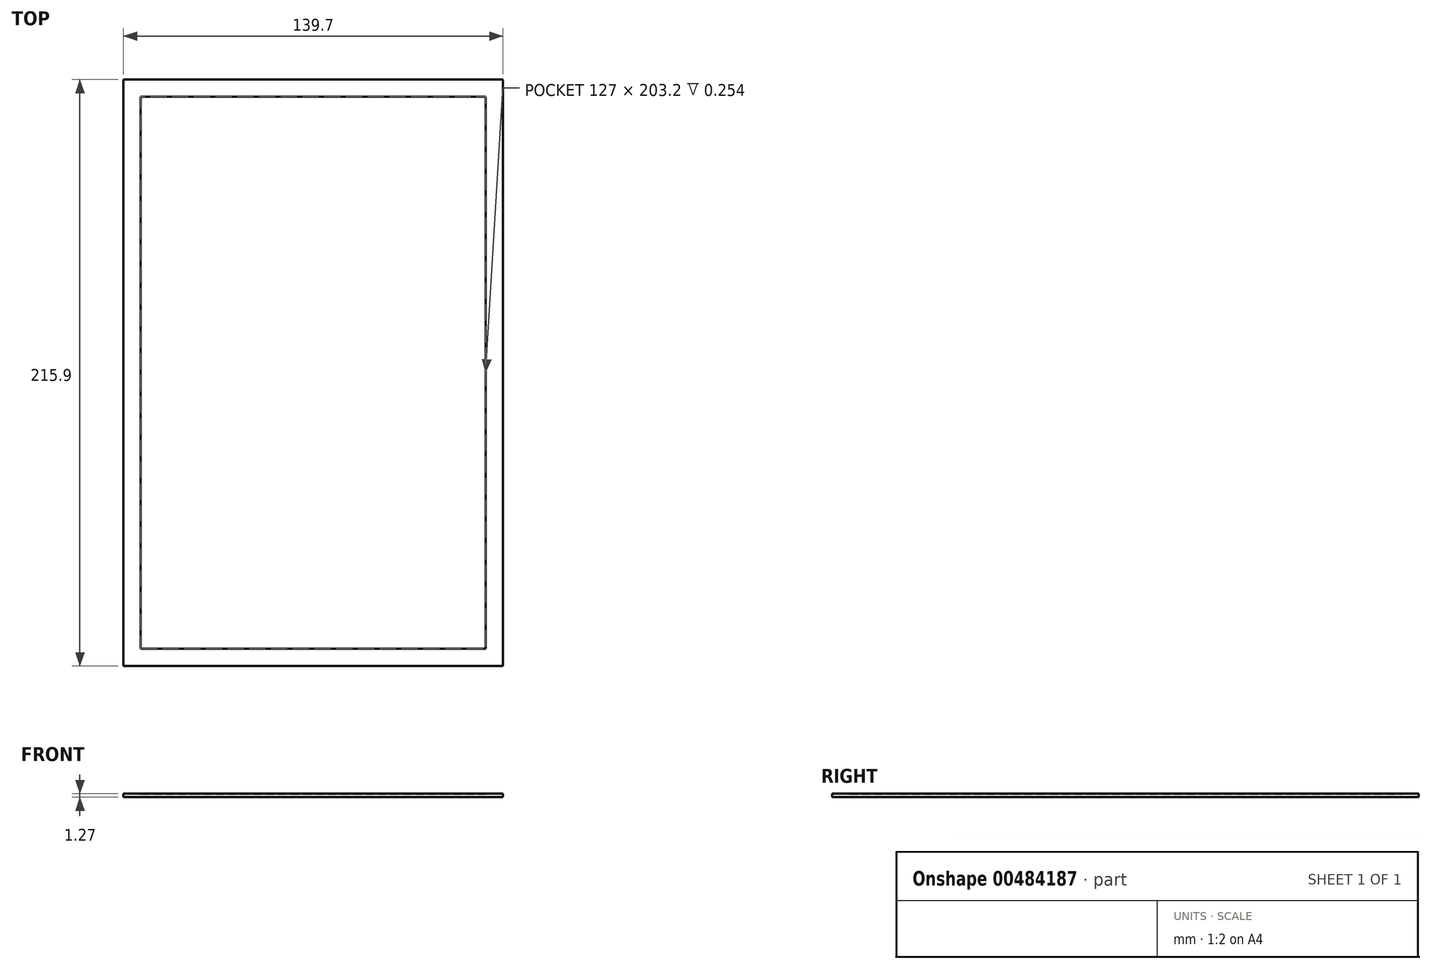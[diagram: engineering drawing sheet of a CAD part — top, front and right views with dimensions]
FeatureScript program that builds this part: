
annotation { "Feature Type Name" : "Feature", "Feature Type Description" : "" }
export const myFeature = defineFeature(function(context is Context, id is Id, definition is map)
    precondition{}
    {
        {
            var Q0;
            Q0=qCreatedBy(makeId("Top.planeOp"),FACE);
            var sketch = newSketch(context, id + "F0", { "sketchPlane" : qUnion([Q0])});
            skLineSegment(sketch, "E0.bottom", {"start": v(0, 0) * mm, "end": v(-139.7, 0) * mm});
            skLineSegment(sketch, "E0.top", {"start": v(0, 215.9) * mm, "end": v(-139.7, 215.9) * mm});
            skLineSegment(sketch, "E0.left", {"start": v(0, 0) * mm, "end": v(0, 215.9) * mm});
            skLineSegment(sketch, "E0.right", {"start": v(-139.7, 0) * mm, "end": v(-139.7, 215.9) * mm});
            skSolve(sketch);
        }
        {
            var Q0;
            Q0 = qSketchRegion(id + "F0", true);
            extrude(context, id + "F1", {"entities" : qUnion([Q0]), "depth" : 1.27 * mm});
        }
        {
            var Q0;
            Q0=makeQuery(id+"F1.opExtrude","CAP_FACE",FACE,{"disambiguationData":[OSD([sQuery(id+"F0.wireOp",EDGE,"E0.bottom"),sQuery(id+"F0.wireOp",EDGE,"E0.top"),sQuery(id+"F0.wireOp",EDGE,"E0.left"),sQuery(id+"F0.wireOp",EDGE,"E0.right")])],"isStart":false});
            var sketch = newSketch(context, id + "F2", { "sketchPlane" : qUnion([Q0])});
            skLineSegment(sketch, "E1.0", {"start": v(0, 215.9) * mm, "end": v(-139.7, 215.9) * mm, "construction": true});
            skLineSegment(sketch, "E1.1", {"start": v(-139.7, 0) * mm, "end": v(-139.7, 215.9) * mm, "construction": true});
            skLineSegment(sketch, "E1.2", {"start": v(0, 0) * mm, "end": v(0, 215.9) * mm, "construction": true});
            skLineSegment(sketch, "E1.3", {"start": v(0, 0) * mm, "end": v(-139.7, 0) * mm, "construction": true});
            skLineSegment(sketch, "E2.bottom", {"start": v(-133.35, 6.35) * mm, "end": v(-6.35, 6.35) * mm});
            skLineSegment(sketch, "E2.top", {"start": v(-133.35, 209.55) * mm, "end": v(-6.35, 209.55) * mm});
            skLineSegment(sketch, "E2.left", {"start": v(-133.35, 6.35) * mm, "end": v(-133.35, 209.55) * mm});
            skLineSegment(sketch, "E2.right", {"start": v(-6.35, 6.35) * mm, "end": v(-6.35, 209.55) * mm});
            skLineSegment(sketch, "E3", {"start": v(-69.85, 215.9) * mm, "end": v(-69.85, 0) * mm, "construction": true});
            skLineSegment(sketch, "E4", {"start": v(0, 107.95) * mm, "end": v(-139.7, 107.95) * mm, "construction": true});
            skPoint(sketch, "E5", {"position": v(-69.85, 6.35) * mm});
            skPoint(sketch, "E6", {"position": v(-133.35, 107.95) * mm});
            skSolve(sketch);
        }
        {
            var Q0;
            Q0 = qSketchRegion(id + "F2", true);
            extrude(context, id + "F3", {"entities" : qUnion([Q0]), "operationType" : NewBodyOperationType.REMOVE, "oppositeDirection" : true, "depth" : 0.25 * mm});
        }
        {
            var Q0;
            Q0=qCreatedBy(makeId("Top.planeOp"),FACE);
            cPlane(context, id + "F4", {"entities" : qUnion([Q0]), "cplaneType" : CPlaneType.OFFSET, "offset" : 50.8 * mm, "width" : 152.4 * mm, "height" : 152.4 * mm});
        }
    });
